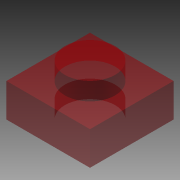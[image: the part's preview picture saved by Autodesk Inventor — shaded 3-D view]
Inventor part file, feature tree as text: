
AUTODESK INVENTOR PART (.ipt)
format: ipt  version: 2013 (Build 170138000, 138)  size: 108,032 bytes
history: native  units: mm
features: extrude x3, sketch x1, pattern_linear x1
ambient origin geometry x8: Origin, YZ Plane, XZ Plane, XY Plane, X Axis, Y Axis, Z Axis, Center Point
bodies: Solid1 (feature_tree)
feature tree (5):
  sketch  "Sketch1"  dims[d0=8.0mm d1=8.0mm d2=4.8mm d3=3.2mm d4=0.0mm d5=4.9mm d6=0.0mm d7=1.7mm d8=0.0mm d9=10.0mm d11=8.0mm d22=10.0mm d24=8.0mm]
  extrude  "Extrusion1"  Depth=8.0mm
  extrude  "Extrusion2"  Depth=4.8mm
  extrude  "Extrusion3"  Depth=3.2mm TaperAngle=0.0deg
  pattern_linear  "Rectangular Pattern1"  Spacing1=4.9mm  [1 undecoded]
note: 1 required parameter value undecoded (feature->parameter linkage not recoverable at this tier; creation-order binding heuristic only, values carry confidence <= 0.55)
